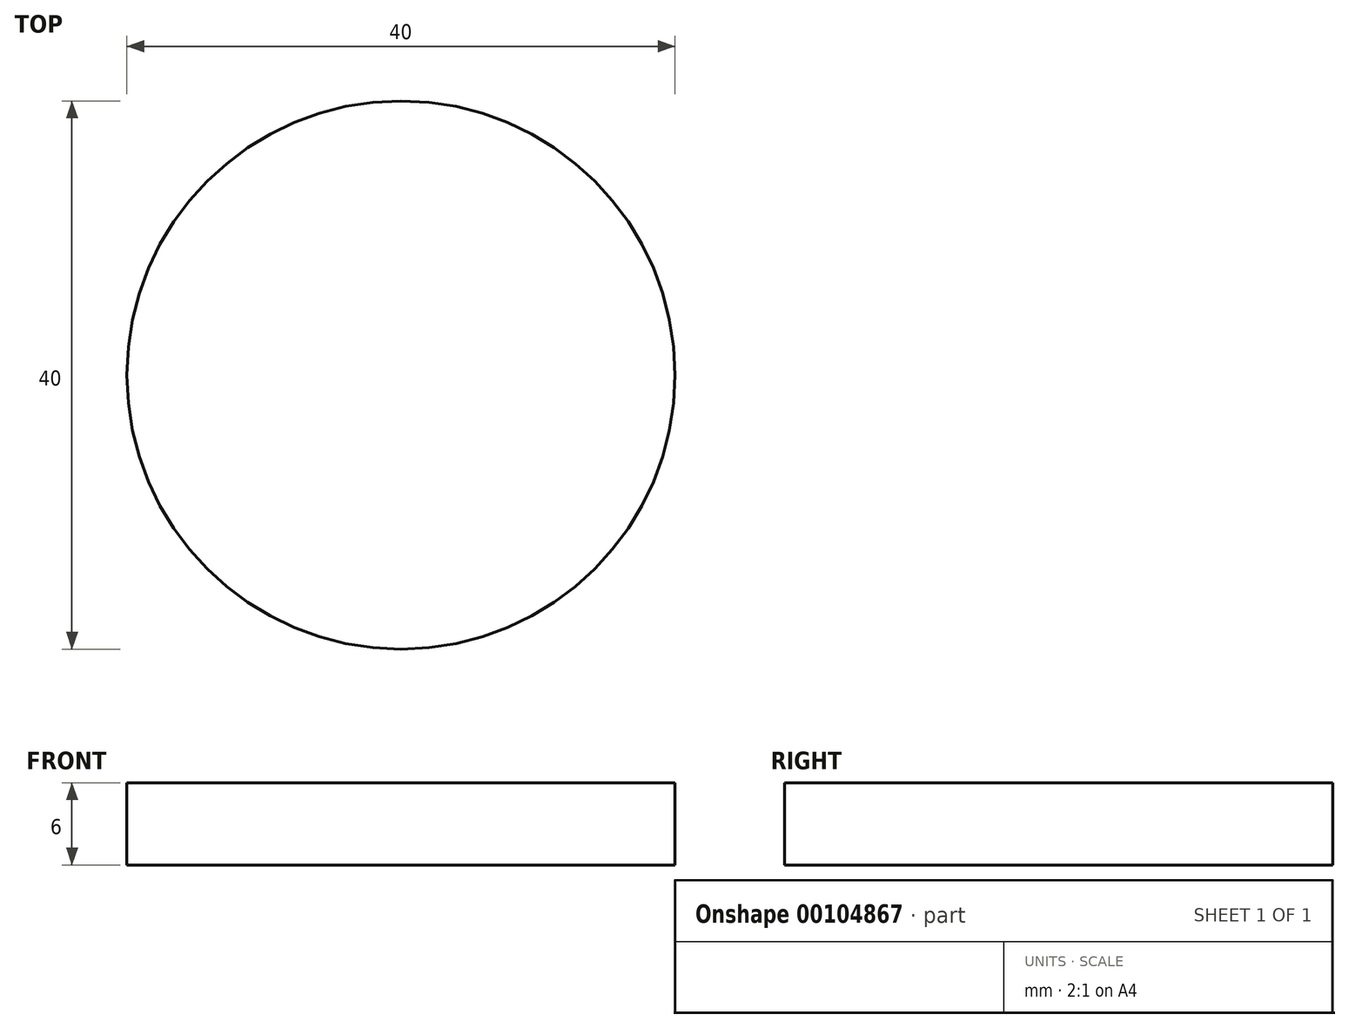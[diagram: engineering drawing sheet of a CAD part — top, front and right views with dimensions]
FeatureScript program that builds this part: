
annotation { "Feature Type Name" : "Feature", "Feature Type Description" : "" }
export const myFeature = defineFeature(function(context is Context, id is Id, definition is map)
    precondition{}
    {
        {
            var Q0;
            Q0=qCreatedBy(makeId("Top.planeOp"),FACE);
            var sketch = newSketch(context, id + "F0", { "sketchPlane" : qUnion([Q0])});
            skCircle(sketch, "E0", {"center": v(0, 0) * mm, "radius": 20 * mm});
            skSolve(sketch);
        }
        {
            var Q0;
            Q0=makeQuery(id+"F0.imprint","IMPRINT",FACE,{"disambiguationData":[TD([[makeQuery(id+"F0.imprint","IMPRINT",EDGE,{"derivedFrom":sQuery(id+"F0.wireOp",EDGE,"E0")}),1.0]])]});
            extrude(context, id + "F1", {"entities" : qUnion([Q0]), "depth" : 6 * mm});
        }
    });
